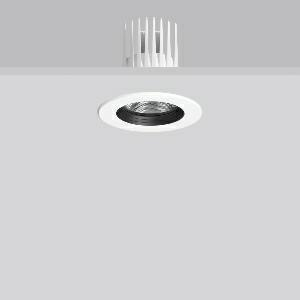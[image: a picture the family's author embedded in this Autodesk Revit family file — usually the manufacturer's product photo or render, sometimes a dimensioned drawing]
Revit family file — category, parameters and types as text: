
# Revit family: heledon_mini_e_901748_002_1_76_ae70
name_source: partatom
category: Lighting Fixtures
units: mm (PartAtom-declared; Revit-internal decimal feet)

## family parameters
Cut with Voids When Loaded = No
Host = Face
Light Source = No
Part Type = Normal
Room Calculation Point = No
Round Connector Dimension = Use Diameter
Shared = No

## types (1)
- HELEDON mini E (1 x LED Modul 940, 3800 lm, 4000)
    Apparent Load = 29 VA
    Approval mark = CE
    CIE Flux Codes = 100 100 100 100 100
    Color Rendering = 92
    Color Temperature = 4000
    Default Elevation = 1800 mm
    Description = Series: HELEDON mini
Round recessed downlight. Housing: die-cast aluminium, powder-coated. Black plastic ring and recessed LED to prevent glare from the side. Optical assembly with reflector made of MIRO-Silver with 98% total light reflection for outstanding efficiency - can be changed without tools. Best colour rendering index Ra>90. Suitable for Recessed ceiling mounting. Installation without tools thanks to spring fastening system. Including separate LED converter with connecting cable 600 mm.High quality converter without flickering and stroboscopic effect. Through-wiring box (5 pole) available as accessory. The following accessories can be mounted without use of tools: interchangeable lenses, decorative glasses, honeycomb louvre, clear and frosted diffusers, white interchangeable plastic ring. 
Colour: traffic white, matt (RAL 9016)
Diameter: 124 mm
Height: 3 mm
Cut-out diameter: 114 mm
Recess height: 170 mm
Luminaire: recess height: 120 mm
Lamp: LED
Socket: without socket
Colour temperature: 4000K
Colour rendering index (CRI): 92
System power: 29 W
Rated luminous flux: 3800 lm
Luminous efficiency: 131 lm/W
Control gear: Converter, dimmable, DALI
Protection class: II
Type of protection: IP 20
    Height = 0 mm  [stored 0 ft]
    Lamp = 1 x LED Modul 940
    Lamp Light Flux = 3800 lm
    Lamp count = 1
    Length = 124 mm  [stored 0.406824 ft]
    Lifetime = 50000 h
    Luminous efficacy = 131 lm/W
    Manufacturer = RZB
    ModVariant = No
    Model = 901748.002.1.76
    Mounting Place = Ceiling
    Mounting Type = Recessed
    Number of Poles = 1
    OnlyDefault = Yes
    Power Factor = 1
    Product Name = HELEDON mini E
    Product group = Recessed downlights
    ProductGroupID = 402
    Protection Class = Protection class II
    Protection Degree = IP 20
    RLX_Detail_Level = 1
    RLX_Emergency_Light_Flux = 0 lm
    RLX_Emergency_Type = 0
    RLX_Emergency_Type_DB = No
    RlxData = <blob elided: 122965 chars, md5=08d9265f>
    Socket = socket
    Standby Power = 0 W
    System Light Flux = 3800 lm
    System Power = 29 W
    Type Comments = Product without accessories
    Type Image = 901657.002.jpg
    URL = http://relux.com
    VarID = ---
    Voltage = 230 V
    Voltage Range = 220-240 V
    Weight = 0.00 kg
    Width = 0 mm  [stored 0 ft]

note: [stored X ft] marks values corroborated as IEEE doubles in the binary element streams (Revit-internal decimal feet)

## geometry (parser evidence)
native form markers: Blend x4, Sweep x12
no freeform markers — native parametric forms only
